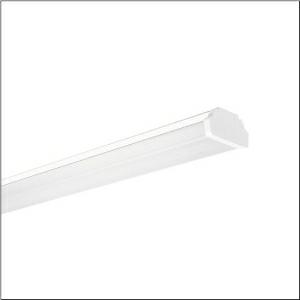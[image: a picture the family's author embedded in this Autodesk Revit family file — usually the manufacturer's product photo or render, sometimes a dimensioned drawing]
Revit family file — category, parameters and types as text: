
# Revit family: dus_31_gen_2_53bd8127v68xc2_dff7
name_source: partatom
category: Lighting Fixtures
units: mm (PartAtom-declared; Revit-internal decimal feet)

## family parameters
Cut with Voids When Loaded = No
Host = Face
Light Source = No
Part Type = Normal
Room Calculation Point = No
Round Connector Dimension = Use Diameter
Shared = No

## types (1)
- DUS 31 Gen.2 (1 x LED, 8340 lm, 47.9 W, 6500K)
    Apparent Load = 48 VA
    CIE Flux Codes = 47 80 95 93 100
    Color Rendering = 80
    Color Temperature = 6500K
    Default Elevation = 1800 mm
    Description = DUS 31 Gen.2, luminaire insert, of sheet steel, coil coated, white, length: 1.535mm, width: 81mm, height: 90mm, 5x system unit, system units: 307mm, LED rated luminous flux: 8.340lm, light colour: 865, SDCM (Standard Deviation of Colour Matching)MacAdam ≤ 3 SDCM (initial), control gear: ON/OFF, control gear: ECG, with plug, 3-pole, with phase selection, mains connection: 220..240V, AC, 50/60Hz, rated input power: 48W, through-wiring accessed according to module size, primary optical cover: cover, of PMMA, light emission: direct distribution, primary light characteristic: symmetric, protection rating (complete): IP20, protection rating (LED compartment): IP50, insulation class (complete): insulation class I (protective earthing), certification: CE, ENEC, VDE, UKCA, impact resistance: IK03, permissible ambient temperature for indoor applications: -35..+45°C, corresponds to IFS (International Featured Standards) requirements for safety and quality in the food industry, reducing of maximum allowable ambient temperature of 5°C with ceiling mounting, packaging unit: 1 piece
    Height = 95 mm
    Lamp = 1 x LED
    Lamp Light Flux = 8340 lm
    Lamp Power = 47.9 W
    Lamp count = 1
    Length = 1535 mm
    Luminous efficacy = 174 lm/W
    Manufacturer = Siteco
    ModVariant = No
    Model = 53BD8127V68XC2
    Mounting Place = Ceiling
    Mounting Type = Pendant
    Number of Poles = 1
    OnlyDefault = Yes
    Power Factor = 1
    Product Name = DUS 31 Gen.2
    Product group = luminaire insert | ceiling pendant
    ProductGroupID = 901
    Protection Class = Protection class I
    Protection Degree = IP 20
    RLX_Detail_Level = 1
    RLX_Emergency_Light_Flux = 0 lm
    RLX_Emergency_Type = 0
    RLX_Emergency_Type_DB = No
    RlxData = <blob elided: 28521 chars, md5=fbf4eef5>
    Socket = socket
    Standby Power = 0 W
    System Light Flux = 8340 lm
    System Power = 48 W
    Type Comments = Product without accessories
    Type Image = l_1319596.jpg
    URL = http://relux.com
    VarID = ---
    Voltage = 0 V
    Weight = 0.00 kg
    Width = 81 mm

## geometry (parser evidence)
native form markers: Blend x4, Sweep x10
no freeform markers — native parametric forms only
